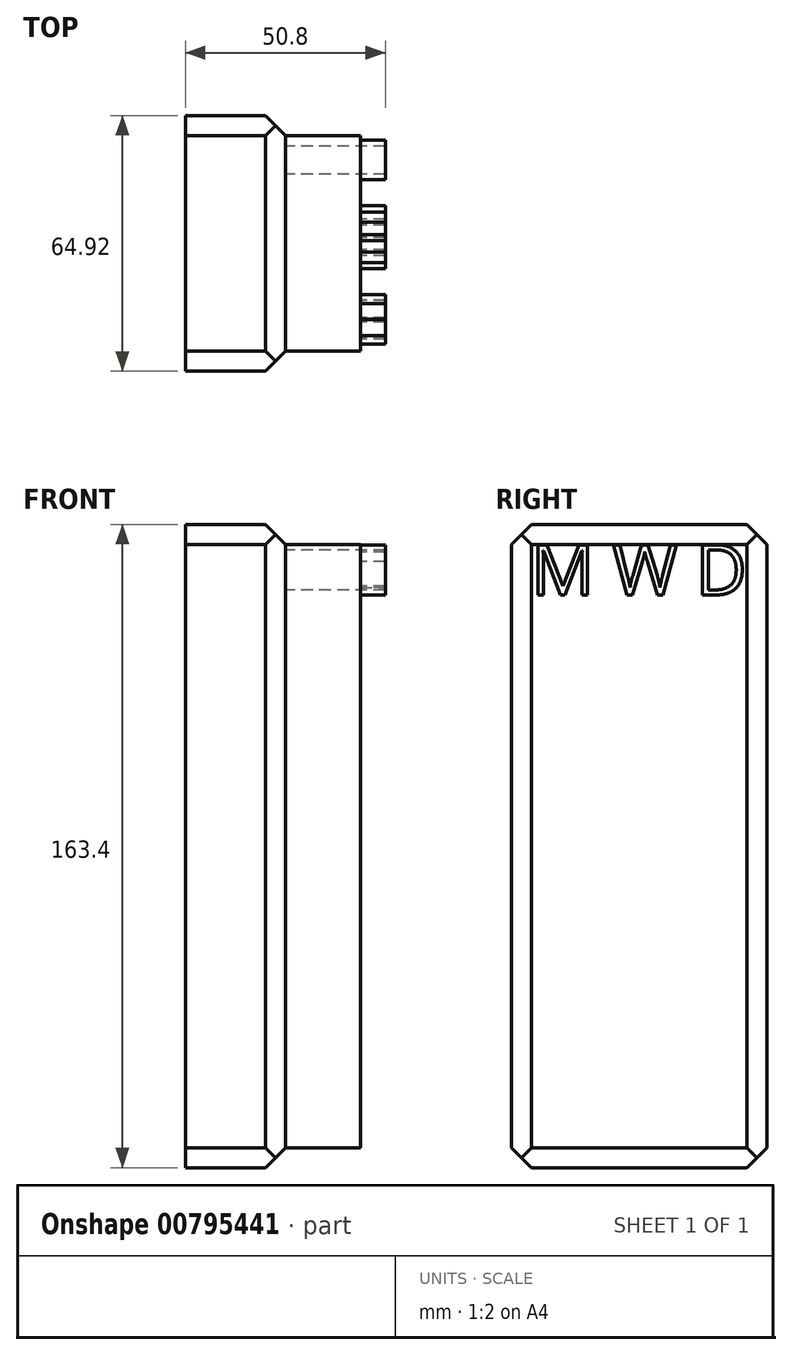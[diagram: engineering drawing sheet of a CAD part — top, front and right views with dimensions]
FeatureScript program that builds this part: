
annotation { "Feature Type Name" : "Feature", "Feature Type Description" : "" }
export const myFeature = defineFeature(function(context is Context, id is Id, definition is map)
    precondition{}
    {
        {
            var Q0;
            Q0=qCreatedBy(makeId("Right.planeOp"),FACE);
            var sketch = newSketch(context, id + "F0", { "sketchPlane" : qUnion([Q0])});
            skLineSegment(sketch, "E0", {"start": v(39.52, 0) * mm, "end": v(39.52, 60.23) * mm});
            skLineSegment(sketch, "E1", {"start": v(39.52, 60.23) * mm, "end": v(0, 60.23) * mm});
            skLineSegment(sketch, "E2", {"start": v(0, 60.23) * mm, "end": v(0, 0) * mm});
            skLineSegment(sketch, "E3", {"start": v(0, 0) * mm, "end": v(39.52, 0) * mm});
            skLineSegment(sketch, "E4", {"start": v(19.76, 134.27) * mm, "end": v(99.34, 168.78) * mm});
            skPoint(sketch, "E4.startSnap0", {"position": v(19.76, 60.23) * mm});
            skSolve(sketch);
        }
        {
            var Q0;
            Q0 = qSketchRegion(id + "F0", true);
            extrude(context, id + "F1", {"entities" : qUnion([Q0]), "depth" : 25.4 * mm, "offsetDistance" : 25.4 * mm});
        }
        {
            var Q0;
            Q0=makeQuery(id+"F1.opExtrude","SWEPT_FACE",FACE,{"disambiguationData":[OSD([sQuery(id+"F0.wireOp",EDGE,"E3")])]});
            extrude(context, id + "F2", {"entities" : qUnion([Q0]), "operationType" : NewBodyOperationType.ADD, "depth" : 103.17 * mm, "offsetDistance" : 25.4 * mm});
        }
        {
            var Q0;
            {var subQ0=sQuery(id+"F0.wireOp",EDGE,"E0");Q0=makeQuery(id+"F2.boolean.opBoolean","MERGE",FACE,{"derivedFrom":[makeQuery(id+"F1.opExtrude","SWEPT_FACE",FACE,{"disambiguationData":[OSD([subQ0])]}),makeQuery(id+"F2.opExtrude","SWEPT_FACE",FACE,{"disambiguationData":[OSD([subQ0,sQuery(id+"F0.wireOp",EDGE,"E3")])]})]});}
            extrude(context, id + "F3", {"entities" : qUnion([Q0]), "operationType" : NewBodyOperationType.ADD, "depth" : 25.4 * mm, "offsetDistance" : 25.4 * mm});
        }
        {
            var Q0;
            {var subQ0=sQuery(id+"F0.wireOp",EDGE,"E3");var subQ1=sQuery(id+"F0.wireOp",EDGE,"E0");Q0=makeQuery(id+"F3.opExtrude","CAP_EDGE",EDGE,{"disambiguationData":[OSD([subQ1,subQ0]),TDD([makeQuery(id+"F2.opExtrude","CAP_EDGE",EDGE,{"disambiguationData":[OSD([subQ1,subQ0])],"isStart":false})])],"isStart":false});}
            chamfer(context, id + "F4", {"entities" : qUnion([Q0]), "width" : 5.08 * mm, "tangentPropagation" : true});
        }
        {
            var Q0;
            {var subQ0=sQuery(id+"F0.wireOp",EDGE,"E3");var subQ1=sQuery(id+"F0.wireOp",EDGE,"E0");Q0=makeQuery(id+"F3.opExtrude","CAP_EDGE",EDGE,{"disambiguationData":[OSD([subQ1,subQ0]),TDD([makeQuery(id+"F2.boolean.opBoolean","MERGE",EDGE,{"derivedFrom":[makeQuery(id+"F1.opExtrude","CAP_EDGE",EDGE,{"disambiguationData":[OSD([subQ1])],"isStart":false}),makeQuery(id+"F2.opExtrude","SWEPT_EDGE",EDGE,{"disambiguationData":[OSD([subQ1,subQ0]),TDD([makeQuery(id+"F1.opExtrude","CAP_VERTEX",VERTEX,{"disambiguationData":[OSD([subQ1,subQ0])],"isStart":false})])]})]})])],"isStart":false});}
            chamfer(context, id + "F5", {"entities" : qUnion([Q0]), "width" : 5.08 * mm, "tangentPropagation" : true});
        }
        {
            var Q0;
            Q0=makeQuery(id+"F3.opExtrude","CAP_EDGE",EDGE,{"disambiguationData":[OSD([sQuery(id+"F0.wireOp",EDGE,"E0"),sQuery(id+"F0.wireOp",EDGE,"E1")])],"isStart":false});
            chamfer(context, id + "F6", {"entities" : qUnion([Q0]), "width" : 5.08 * mm, "tangentPropagation" : true});
        }
        {
            var Q0;
            {var subQ0=sQuery(id+"F0.wireOp",EDGE,"E3");var subQ1=sQuery(id+"F0.wireOp",EDGE,"E0");Q0=makeQuery(id+"F3.boolean.opBoolean","MERGE",EDGE,{"derivedFrom":[makeQuery(id+"F2.opExtrude","CAP_EDGE",EDGE,{"disambiguationData":[OSD([subQ0]),TDD([makeQuery(id+"F1.opExtrude","CAP_EDGE",EDGE,{"disambiguationData":[OSD([subQ0])],"isStart":false})])],"isStart":false}),makeQuery(id+"F3.opExtrude","SWEPT_EDGE",EDGE,{"disambiguationData":[OSD([subQ1,subQ0]),TDD([makeQuery(id+"F2.opExtrude","CAP_VERTEX",VERTEX,{"disambiguationData":[OSD([subQ1,subQ0]),TDD([makeQuery(id+"F1.opExtrude","CAP_VERTEX",VERTEX,{"disambiguationData":[OSD([subQ1,subQ0])],"isStart":false})])],"isStart":false})])]})]});}
            chamfer(context, id + "F7", {"entities" : qUnion([Q0]), "width" : 5.08 * mm, "tangentPropagation" : true});
        }
        {
            var Q0;
            {var subQ0=sQuery(id+"F0.wireOp",EDGE,"E1");var subQ1=sQuery(id+"F0.wireOp",EDGE,"E0");Q0=makeQuery(id+"F3.boolean.opBoolean","MERGE",EDGE,{"derivedFrom":[makeQuery(id+"F1.opExtrude","CAP_EDGE",EDGE,{"disambiguationData":[OSD([subQ0])],"isStart":false}),makeQuery(id+"F3.opExtrude","SWEPT_EDGE",EDGE,{"disambiguationData":[OSD([subQ1,subQ0]),TDD([makeQuery(id+"F1.opExtrude","CAP_VERTEX",VERTEX,{"disambiguationData":[OSD([subQ1,subQ0])],"isStart":false})])]})]});}
            chamfer(context, id + "F8", {"entities" : qUnion([Q0]), "width" : 5.08 * mm, "tangentPropagation" : true});
        }
        {
            var Q0;
            {var subQ0=sQuery(id+"F0.wireOp",EDGE,"E3");var subQ1=sQuery(id+"F0.wireOp",EDGE,"E2");Q0=makeQuery(id+"F2.boolean.opBoolean","MERGE",EDGE,{"derivedFrom":[makeQuery(id+"F1.opExtrude","CAP_EDGE",EDGE,{"disambiguationData":[OSD([subQ1])],"isStart":false}),makeQuery(id+"F2.opExtrude","SWEPT_EDGE",EDGE,{"disambiguationData":[OSD([subQ1,subQ0]),TDD([makeQuery(id+"F1.opExtrude","CAP_VERTEX",VERTEX,{"disambiguationData":[OSD([subQ1,subQ0])],"isStart":false})])]})]});}
            chamfer(context, id + "F9", {"entities" : qUnion([Q0]), "width" : 5.08 * mm, "tangentPropagation" : true});
        }
        {
            var Q0;
            Q0=makeQuery(id+"F2.opExtrude","CAP_EDGE",EDGE,{"disambiguationData":[OSD([sQuery(id+"F0.wireOp",EDGE,"E2"),sQuery(id+"F0.wireOp",EDGE,"E3")])],"isStart":false});
            chamfer(context, id + "F10", {"entities" : qUnion([Q0]), "width" : 5.08 * mm, "tangentPropagation" : true});
        }
        {
            var Q0;
            Q0=makeQuery(id+"F1.opExtrude","SWEPT_EDGE",EDGE,{"disambiguationData":[OSD([sQuery(id+"F0.wireOp",EDGE,"E1"),sQuery(id+"F0.wireOp",EDGE,"E2")])]});
            chamfer(context, id + "F11", {"entities" : qUnion([Q0]), "width" : 5.08 * mm, "tangentPropagation" : true});
        }
        {
            var Q0;
            {var subQ0=sQuery(id+"F0.wireOp",EDGE,"E3");var subQ1=sQuery(id+"F0.wireOp",EDGE,"E0");Q0=makeQuery(id+"F3.boolean.opBoolean","MERGE",FACE,{"derivedFrom":[makeQuery(id+"F2.boolean.opBoolean","MERGE",FACE,{"derivedFrom":[makeQuery(id+"F1.opExtrude","CAP_FACE",FACE,{"disambiguationData":[OSD([subQ1,sQuery(id+"F0.wireOp",EDGE,"E1"),sQuery(id+"F0.wireOp",EDGE,"E2"),subQ0])],"isStart":false}),makeQuery(id+"F2.opExtrude","SWEPT_FACE",FACE,{"disambiguationData":[OSD([subQ0]),TDD([makeQuery(id+"F1.opExtrude","CAP_EDGE",EDGE,{"disambiguationData":[OSD([subQ0])],"isStart":false})])]})]}),makeQuery(id+"F3.opExtrude","SWEPT_FACE",FACE,{"disambiguationData":[OSD([subQ1,subQ0]),TDD([makeQuery(id+"F2.boolean.opBoolean","MERGE",EDGE,{"derivedFrom":[makeQuery(id+"F1.opExtrude","CAP_EDGE",EDGE,{"disambiguationData":[OSD([subQ1])],"isStart":false}),makeQuery(id+"F2.opExtrude","SWEPT_EDGE",EDGE,{"disambiguationData":[OSD([subQ1,subQ0]),TDD([makeQuery(id+"F1.opExtrude","CAP_VERTEX",VERTEX,{"disambiguationData":[OSD([subQ1,subQ0])],"isStart":false})])]})]})])]})]});}
            var sketch = newSketch(context, id + "F12", { "sketchPlane" : qUnion([Q0])});
            skText(sketch, "E5", { "text": "M W D", "fontName": "OpenSans-Regular.ttf"});
            const initialGuessF12  = {"E5": [0.00508, 0.04235, 1, 0, 0.0128]};
            skSetInitialGuess(sketch, initialGuessF12);
            skSolve(sketch);
        }
        {
            var Q0;
            Q0 = qSketchRegion(id + "F12", true);
            extrude(context, id + "F13", {"entities" : qUnion([Q0]), "operationType" : NewBodyOperationType.ADD, "depth" : 25.4 * mm, "offsetDistance" : 25.4 * mm});
        }
        {
            var Q0;
            {var subQ0=sQuery(id+"F0.wireOp",EDGE,"E1");var subQ1=sQuery(id+"F0.wireOp",EDGE,"E0");var subQ2=sQuery(id+"F0.wireOp",EDGE,"E3");var subQ3=sQuery(id+"F0.wireOp",EDGE,"E2");Q0=makeQuery(id+"F13.boolean.opBoolean","SPLIT",FACE,{"disambiguationData":[TD([makeQuery(id+"F13.opExtrude","SWEPT_FACE",FACE,{"disambiguationData":[OSD([sQuery(id+"F12.wireOp",EDGE,"E5.sketch_text.stroke-0")])]})])],"derivedFrom":makeQuery(id+"F3.boolean.opBoolean","MERGE",FACE,{"derivedFrom":[makeQuery(id+"F2.boolean.opBoolean","MERGE",FACE,{"derivedFrom":[makeQuery(id+"F1.opExtrude","CAP_FACE",FACE,{"disambiguationData":[OSD([subQ1,subQ0,subQ3,subQ2])],"isStart":false}),makeQuery(id+"F2.opExtrude","SWEPT_FACE",FACE,{"disambiguationData":[OSD([subQ2]),TDD([makeQuery(id+"F1.opExtrude","CAP_EDGE",EDGE,{"disambiguationData":[OSD([subQ2])],"isStart":false})])]})]}),makeQuery(id+"F3.opExtrude","SWEPT_FACE",FACE,{"disambiguationData":[OSD([subQ1,subQ2]),TDD([makeQuery(id+"F2.boolean.opBoolean","MERGE",EDGE,{"derivedFrom":[makeQuery(id+"F1.opExtrude","CAP_EDGE",EDGE,{"disambiguationData":[OSD([subQ1])],"isStart":false}),makeQuery(id+"F2.opExtrude","SWEPT_EDGE",EDGE,{"disambiguationData":[OSD([subQ1,subQ2]),TDD([makeQuery(id+"F1.opExtrude","CAP_VERTEX",VERTEX,{"disambiguationData":[OSD([subQ1,subQ2])],"isStart":false})])]})]})])]})]})});}
            extrude(context, id + "F14", {"entities" : qUnion([Q0]), "operationType" : NewBodyOperationType.ADD, "depth" : 19.05 * mm, "offsetDistance" : 25.4 * mm});
        }
    });
